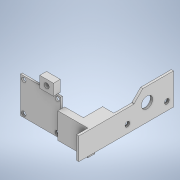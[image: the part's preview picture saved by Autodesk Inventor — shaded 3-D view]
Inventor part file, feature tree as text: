
AUTODESK INVENTOR PART (.ipt)
format: ipt  version: 2020.2 (Build 242310000, 310)  size: 334,848 bytes
history: native  units: mm
features: sketch x16, extrude x13, hole x4, projected_geometry x2
ambient origin geometry x8: Origin, YZ Plane, XZ Plane, XY Plane, X Axis, Y Axis, Z Axis, Center Point
bodies: Body1 (feature_tree)
feature tree (35):
  extrude  "Extrusion7"  Depth=6.08mm
  hole  "Hole4"  [1 undecoded]
  sketch  "Sketch16"  dims[d70=12.16mm d71=10.0mm]
  extrude  "Extrusion8"  Depth=10.0mm
  hole  "Hole5"  [1 undecoded]
  extrude  "Extrusion9"  Depth=32.05mm
  extrude  "Extrusion10"  Depth=32.05mm
  extrude  "Extrusion11"  Depth=3.0mm
  hole  "Hole6"  [1 undecoded]
  hole  "Hole7"  [1 undecoded]
  extrude  "Extrusion13"  Depth=26.05mm
  extrude  "Extrusion14"  Depth=4.0mm TaperAngle=0.0deg
  extrude  "Extrusion15"  Depth=10.0mm
  extrude  "Extrusion16"  TaperAngle=90.0deg  [1 undecoded]
  extrude  "Extrusion17"  TaperAngle=90.0deg  [1 undecoded]
  extrude  "Extrusion18"  Depth=10.0mm
  extrude  "Extrusion19"  Depth=2.5mm TaperAngle=0.0deg
  extrude  "Extrusion20"  Depth=10.0mm
  sketch  "Sketch14"  dims[d66=6.08mm d67=6.08mm]
  sketch  "Sketch15"  dims[d68=5.0mm d69=90.0deg]
  sketch  "Sketch17"  dims[d72=2.0mm d73=0.0mm]
  projected_geometry  "Projected Loop2"
  sketch  "Sketch18"  dims[d74=4.5mm d75=6.0mm d76=9.4mm d77=2.0mm d78=90.0deg d79=8.0mm d80=20.594885mm d81=10.0mm]
  projected_geometry  "Projected Loop3"
  sketch  "Sketch19"  dims[d82=35.7mm d83=32.05mm]
  sketch  "Sketch21"  dims[d84=35.7mm d85=32.05mm]
  sketch  "Sketch22"  dims[d86=3.0mm d87=3.0mm]
  sketch  "Sketch23"  dims[d88=29.7mm d89=26.05mm]
  sketch  "Sketch24"  dims[d90=3.0mm d91=3.0mm]
  sketch  "Sketch25"  dims[d92=29.7mm d93=26.05mm]
  sketch  "Sketch26"  dims[d94=1.5mm d95=0.0mm]
  sketch  "Sketch27"  dims[d96=3.9mm d97=6.0mm d98=8.2mm d99=2.0mm d100=90.0deg d101=8.0mm d102=20.594885mm d103=4.0mm d104=0.0mm]
  sketch  "Sketch28"  dims[d105=30.0mm d106=0.0mm d107=10.0mm]
  sketch  "Sketch29"  dims[d108=50.0mm d109=90.0deg]
  sketch  "Sketch30"  dims[d110=45.0mm d111=90.0deg d112=25.0mm d113=2.5mm d114=0.0mm d118=14.05mm d119=90.0deg d120=6.713mm d121=90.0deg d122=10.0mm d123=6.0mm d124=8.2mm d125=2.0mm d126=90.0deg d127=8.0mm d128=20.594885mm d129=8.0mm d130=90.0deg d131=17.5mm d132=90.0deg d133=35.0mm d134=4.2mm d135=6.0mm d136=8.2mm d137=2.0mm d138=90.0deg d139=8.0mm d140=20.594885mm d141=9.0mm d142=90.0deg d145=35.0mm d146=0.0mm d147=11.0mm d148=135.0deg d149=20.0mm d150=35.0mm d151=0.0mm d152=20.0mm d153=90.0deg d154=90.0deg d155=11.45mm d156=4.669mm d157=90.0deg d158=8.0mm d159=17.5mm d160=35.0mm d161=4.2mm d162=4.2mm d163=10.0mm d164=2.0mm d165=0.0mm d166=2.0mm d167=0.0mm d168=35.0mm d169=2.0mm d170=10.0mm d171=0.0mm d172=10.0mm d173=40.0mm d174=10.0mm d175=0.0mm d176=10.0mm d177=0.0mm d178=10.0mm d179=0.0mm d180=12.16mm d181=10.0mm d182=0.0mm d183=16.0mm d184=10.0mm d185=0.0mm]
note: 6 required parameter values undecoded (feature->parameter linkage not recoverable at this tier; creation-order binding heuristic only, values carry confidence <= 0.55)
